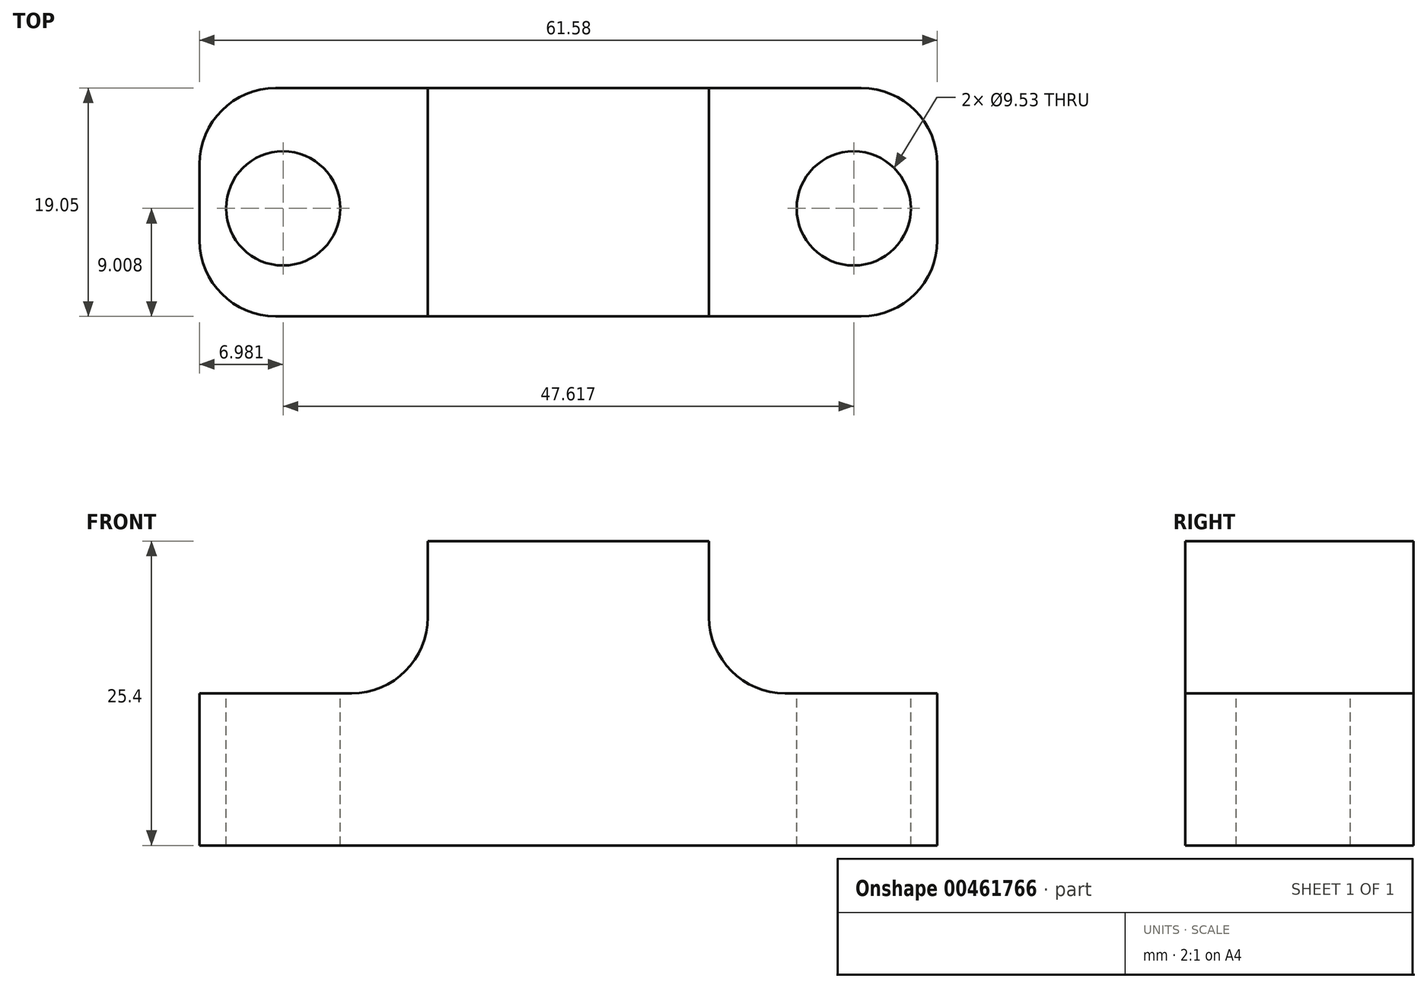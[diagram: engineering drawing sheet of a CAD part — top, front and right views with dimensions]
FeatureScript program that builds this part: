
annotation { "Feature Type Name" : "Feature", "Feature Type Description" : "" }
export const myFeature = defineFeature(function(context is Context, id is Id, definition is map)
    precondition{}
    {
        {
            var Q0;
            Q0=qCreatedBy(makeId("Front.planeOp"),FACE);
            var sketch = newSketch(context, id + "F0", { "sketchPlane" : qUnion([Q0])});
            skLineSegment(sketch, "E0", {"start": v(-30.79, 16.8) * mm, "end": v(-30.79, 4.1) * mm});
            skLineSegment(sketch, "E1", {"start": v(-30.79, 4.1) * mm, "end": v(0.96, 4.1) * mm});
            skLineSegment(sketch, "E2", {"start": v(0.96, 4.1) * mm, "end": v(0.96, 29.5) * mm});
            skLineSegment(sketch, "E3", {"start": v(0.96, 29.5) * mm, "end": v(-11.74, 29.5) * mm});
            skLineSegment(sketch, "E4", {"start": v(-30.79, 16.8) * mm, "end": v(-11.74, 16.8) * mm});
            skLineSegment(sketch, "E5", {"start": v(-11.74, 16.8) * mm, "end": v(-11.74, 29.5) * mm});
            skSolve(sketch);
        }
        {
            var Q0;
            Q0=makeQuery(id+"F0.imprint","IMPRINT",FACE,{"disambiguationData":[TD([[makeQuery(id+"F0.imprint","IMPRINT",EDGE,{"derivedFrom":sQuery(id+"F0.wireOp",EDGE,"E0")}),1.0]])]});
            extrude(context, id + "F1", {"entities" : qUnion([Q0]), "depth" : 19.05 * mm});
        }
        {
            var Q0;
            Q0=makeQuery(id+"F1.opExtrude","CAP_EDGE",EDGE,{"disambiguationData":[OSD([sQuery(id+"F0.wireOp",EDGE,"E0")])],"isStart":true});
            var Q1;
            Q1=makeQuery(id+"F1.opExtrude","CAP_EDGE",EDGE,{"disambiguationData":[OSD([sQuery(id+"F0.wireOp",EDGE,"E0")])],"isStart":false});
            var Q2;
            Q2=makeQuery(id+"F1.opExtrude","SWEPT_EDGE",EDGE,{"disambiguationData":[OSD([sQuery(id+"F0.wireOp",EDGE,"E4"),sQuery(id+"F0.wireOp",EDGE,"E5")])]});
            fillet(context, id + "F2", {"entities" : qUnion([Q0, Q1, Q2]), "radius" : 6.35 * mm, "tangentPropagation" : true, "allowEdgeOverflow" : false});
        }
        {
            var Q0;
            Q0=makeQuery(id+"F1.opExtrude","SWEPT_FACE",FACE,{"disambiguationData":[OSD([sQuery(id+"F0.wireOp",EDGE,"E4")])]});
            var sketch = newSketch(context, id + "F3", { "sketchPlane" : qUnion([Q0])});
            skCircle(sketch, "E6", {"center": v(-23.8, -10.04) * mm, "radius": 3.62 * mm});
            skSolve(sketch);
        }
        {
            var Q0;
            Q0=sQuery(id+"F3.wireOp",VERTEX,"E6.center");
            var Q1;
            Q1=makeQuery(id+"F1.opExtrude","SWEPT_BODY",BODY,{"disambiguationData":[OSD([sQuery(id+"F0.wireOp",EDGE,"E0"),sQuery(id+"F0.wireOp",EDGE,"E1"),sQuery(id+"F0.wireOp",EDGE,"E2"),sQuery(id+"F0.wireOp",EDGE,"E3"),sQuery(id+"F0.wireOp",EDGE,"E4"),sQuery(id+"F0.wireOp",EDGE,"E5")])]});
            hole(context, id + "F4", {"style" : HoleStyle.SIMPLE, "endStyle" : HoleEndStyle.THROUGH, "holeDiameter" : 9.52 * mm, "isTappedThrough" : true, "tappedDepth" : 12.7 * mm, "tapClearance" : 3, "locations" : qUnion([Q0]), "scope" : qUnion([Q1])});
        }
        {
            var Q0;
            Q0=makeQuery(id+"F1.opExtrude","SWEPT_BODY",BODY,{"disambiguationData":[OSD([sQuery(id+"F0.wireOp",EDGE,"E0"),sQuery(id+"F0.wireOp",EDGE,"E1"),sQuery(id+"F0.wireOp",EDGE,"E2"),sQuery(id+"F0.wireOp",EDGE,"E3"),sQuery(id+"F0.wireOp",EDGE,"E4"),sQuery(id+"F0.wireOp",EDGE,"E5")])]});
            var Q1;
            Q1=qCreatedBy(makeId("Right.planeOp"),FACE);
            mirror(context, id + "F5", {"operationType" : NewBodyOperationType.ADD, "entities" : qUnion([Q0]), "mirrorPlane" : qUnion([Q1])});
        }
    });
